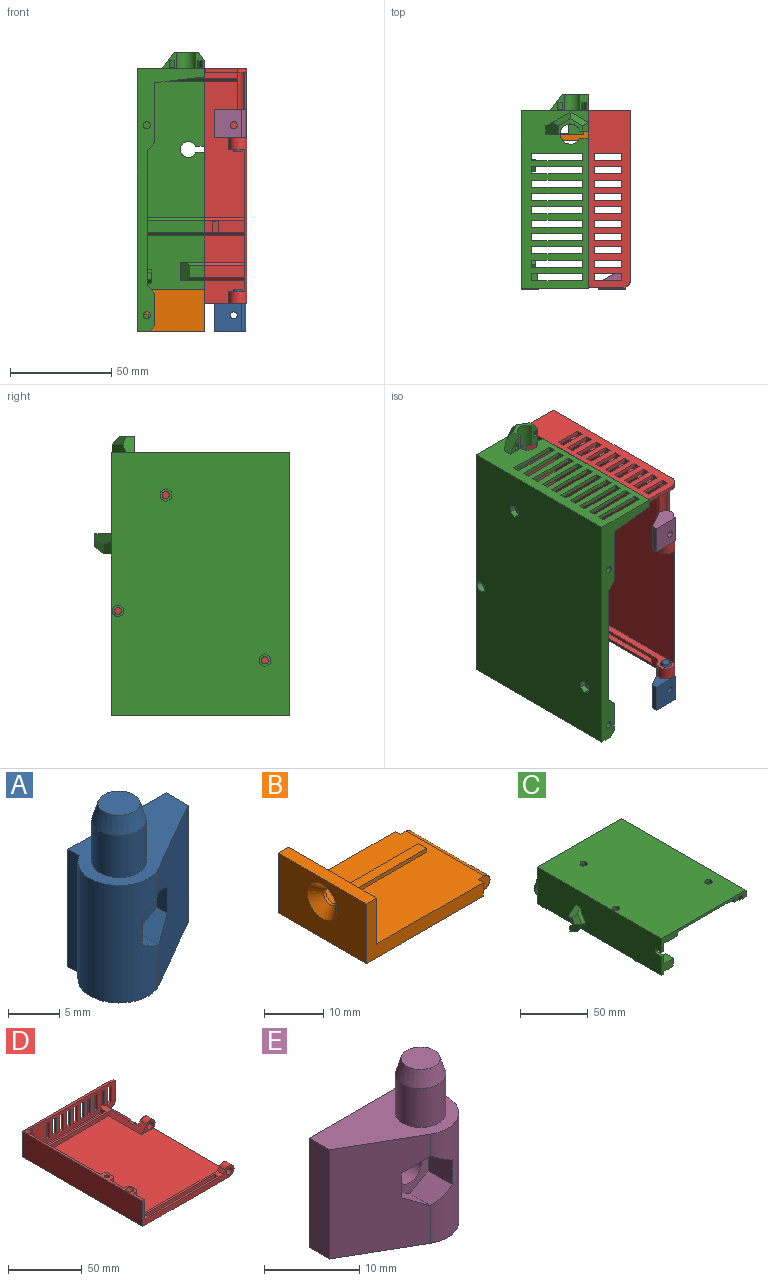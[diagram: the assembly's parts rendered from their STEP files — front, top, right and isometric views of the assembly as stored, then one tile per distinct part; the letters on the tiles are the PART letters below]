
ASSEMBLY  parts=5 mates=4
PART A: 18 faces, bbox 15.5x9x21 mm
  f0: cylinder r=4mm len=14mm, axis (0,0,1), area 161.7mm2, adj f1,f2,f5,f6,f11,f12,f15,f16
  f1: plane 14x9.51mm, normal (0.5,-0.87,0), area 138.4mm2, adj f0,f4,f5,f6,f12,f13,f14,f15
  f2: plane 14x1.55mm, normal (-1,0,0), area 21.7mm2, adj f0,f3,f5,f6
  f3: plane 14x13.53mm, normal (0,1,0), area 179.8mm2, adj f2,f4,f5,f6,f10
  f4: plane 14x3mm, normal (1,0,0), area 42mm2, adj f1,f3,f5,f6
  f5: plane 15.5x9mm, normal (0,0,-1), area 99.6mm2, adj f0,f1,f2,f3,f4
  f6: plane 15.5x9mm, normal (0,0,1), area 77.6mm2, adj f0,f1,f2,f3,f4,f7
  f7: cylinder r=2.65mm len=5.3mm, axis (0,0,-1), area 83.3mm2, adj f6,f9
  f8: plane 4.1x4.1mm, normal (0,0,1), area 13.2mm2, adj f9
  f9: cone r=2.05mm half-angle=16.7deg, axis (0,0,-1), area 30.8mm2, adj f7,f8
  f10: cylinder r=1.75mm len=5.41mm, axis (0,-1,0), area 59.5mm2, adj f3,f17
  f11: plane 3.52x3.18mm, normal (1,0,0.01), area 11.2mm2, adj f0,f12,f16,f17
  f12: plane 3.59x2.76mm, normal (0.5,0,0.87), area 11mm2, adj f0,f1,f11,f13,f17
  f13: plane 3.04x2.74mm, normal (-0.5,0,0.86), area 7.2mm2, adj f1,f12,f14,f17
  f14: plane 3.18x1.48mm, normal (-1,0,-0.01), area 4.7mm2, adj f1,f13,f15,f17
  f15: plane 3.06x2.76mm, normal (-0.5,0,-0.87), area 7.2mm2, adj f0,f1,f14,f16,f17
  f16: plane 3.59x2.74mm, normal (0.5,0,-0.86), area 11mm2, adj f0,f11,f15,f17
  f17: plane 6.35x5.52mm, normal (0,-1,0), area 16.6mm2, adj f10,f11,f12,f13,f14,f15,f16
PART B: 19 faces, bbox 30.7x21x12.3 mm
  f0: plane 26.8x21mm, normal (0,0,1), area 525mm2, adj f1,f2,f3,f5,f6,f7,f9,f10
  f1: plane 2.8x2.8mm, normal (0,1,0), area 7mm2, adj f0,f2,f8,f18
  f2: plane 2.8x1.2mm, normal (1,0,0), area 3.4mm2, adj f0,f1,f3,f8
  f3: plane 27.9x12.3mm, normal (0,1,0), area 101.9mm2, adj f0,f2,f4,f8,f14,f15
  f4: plane 21x12.3mm, normal (-1,0,0), area 219.8mm2, adj f3,f5,f8,f15,f17
  f5: plane 27.9x12.3mm, normal (0,-1,0), area 101.9mm2, adj f0,f4,f6,f8,f14,f15
  f6: plane 2.8x1.2mm, normal (1,0,0), area 3.4mm2, adj f0,f5,f7,f8
  f7: plane 2.8x2.8mm, normal (0,-1,0), area 7mm2, adj f0,f6,f8,f18
  f8: plane 29.3x21mm, normal (0,0,-1), area 611.9mm2, adj f1,f2,f3,f4,f5,f6,f7,f18
  f9: plane 17.2x0.8mm, normal (0,1,0), area 13.8mm2, adj f0,f10,f12,f13
  f10: plane 2x0.8mm, normal (-1,0,0), area 1.6mm2, adj f0,f9,f11,f13
  f11: plane 17.2x0.8mm, normal (0,-1,0), area 13.8mm2, adj f0,f10,f12,f13
  f12: plane 2x0.8mm, normal (1,0,0), area 1.6mm2, adj f0,f9,f11,f13
  f13: plane 17.2x2mm, normal (0,0,1), area 34.4mm2, adj f9,f10,f11,f12
  f14: plane 21x9.5mm, normal (1,0,0), area 191.5mm2, adj f0,f3,f5,f15,f16
  f15: plane 21x2.5mm, normal (0,0,1), area 52.5mm2, adj f3,f4,f5,f14
  f16: cylinder r=1.6mm len=3.2mm, axis (1,0,0), area 6mm2, adj f14,f17
  f17: cone r=1.6mm half-angle=45deg, axis (-1,0,0), area 43.1mm2, adj f4,f16
  f18: cylinder r=1.4mm len=18.6mm, axis (0,-1,0), area 81.8mm2, adj f0,f1,f7,f8
PART C: 219 faces, bbox 96x138x36.3 mm
  f0: plane 14.2x3.4mm, normal (0,-1,0), area 39.1mm2, adj f1,f3,f5,f205,f213,f214,f215
  f1: plane 14.2x5mm, normal (0,0,-1), area 55mm2, adj f0,f5,f205,f206,f214,f215,f216
  f2: plane 14.2x3.4mm, normal (0,1,0), area 39.1mm2, adj f3,f5,f207,f208,f209,f210,f211
  f3: plane 82x22.75mm, normal (0,0,-1), area 1628.8mm2, adj f0,f2,f4,f5,f11,f18,f154,f155
  f4: plane 88x12.75mm, normal (0,-1,0), area 261.8mm2, adj f3,f5,f11,f22,f30,f32,f140,f189
  f5: plane 47.25x31.3mm, normal (1,0,0), area 1103.9mm2, adj f0,f1,f2,f3,f4,f6,f14,f18
  f6: plane 83x70.25mm, normal (0,0,-1), area 5742.5mm2, adj f5,f7,f13,f14,f16,f142,f146,f149
  f7: plane 67.25x31.3mm, normal (1,0,0), area 2014.9mm2, adj f6,f12,f15,f16,f17,f19,f21,f26
  f8: plane 31.3x13mm, normal (0,-1,0), area 294.7mm2, adj f15,f33,f112,f113,f114,f170
  f9: cylinder r=1.75mm len=4mm, axis (-1,0,0), area 44mm2, adj f11,f32
  f10: cylinder r=1.75mm len=4mm, axis (-1,0,0), area 44mm2, adj f13,f32
  f11: plane 22.75x7.29mm, normal (-1,0,0), area 111.6mm2, adj f3,f4,f9,f18,f139,f140,f141,f154
  f12: plane 82x9mm, normal (0,0,-1), area 474.7mm2, adj f7,f13,f16,f17,f40,f41,f42,f43
  f13: plane 40.5x31.79mm, normal (-1,0,0), area 337.4mm2, adj f6,f10,f12,f15,f17,f25,f27,f33
  f14: plane 83x3mm, normal (0,1,0), area 249mm2, adj f5,f6,f38,f146
  f15: plane 82x14.5mm, normal (0,0,-1), area 1143.9mm2, adj f7,f8,f13,f17,f27,f114,f168,f169
  f16: plane 77x3mm, normal (0,-1,0), area 231mm2, adj f6,f7,f12,f150
  f17: plane 82x3mm, normal (0,1,0), area 246mm2, adj f7,f12,f13,f15
  f18: plane 82x3mm, normal (0,-1,0), area 246mm2, adj f3,f5,f11,f38
  f19: plane 10x4.25mm, normal (0,1,0), area 34.2mm2, adj f7,f21,f127,f131,f135,f136,f137,f138
  f20: plane 8x7mm, normal (0,1,0), area 23.9mm2, adj f22,f127,f131,f134,f135,f136,f137,f138
  f21: plane 88.62x14.5mm, normal (0,0,-1), area 250.1mm2, adj f5,f7,f19,f22,f31,f129,f131,f132
  f22: plane 130x33.3mm, normal (-1,0,0), area 4135.7mm2, adj f4,f20,f21,f25,f26,f30,f31,f127
  f23: plane 12x4.23mm, normal (1,0,0), area 36.5mm2, adj f26,f112,f115,f118,f119,f123,f124,f125
  f24: plane 8x7mm, normal (1,0,0), area 24mm2, adj f25,f112,f118,f122,f123,f124,f125,f126
  f25: plane 88x33.3mm, normal (0,1,0), area 1841.8mm2, adj f13,f22,f24,f26,f30,f32,f33,f73
  f26: plane 42.28x10mm, normal (0,0,-1), area 116.2mm2, adj f7,f22,f23,f25,f115,f116,f119,f128
  f27: plane 64.5x31.3mm, normal (0,-1,0), area 1143.9mm2, adj f13,f15,f33,f73,f74,f75,f76,f77
  f28: cylinder r=1.75mm len=4mm, axis (0,0,1), area 44mm2, adj f58,f65
  f29: cylinder r=1.75mm len=4mm, axis (0,0,1), area 44mm2, adj f51,f72
  f30: plane 130x88mm, normal (0,0,1), area 11361.1mm2, adj f4,f22,f25,f32,f59,f60,f61,f62
  f31: plane 17.05x11.7mm, normal (0,-1,0), area 103.7mm2, adj f5,f21,f22,f190,f200,f201,f204,f217
  f32: plane 130x33.3mm, normal (1,0,0), area 987.5mm2, adj f4,f9,f10,f25,f30,f33,f38,f139
  f33: plane 74.5x4mm, normal (0,0,-1), area 169mm2, adj f8,f13,f25,f27,f32,f113,f114,f145
  f34: plane 7.5x3mm, normal (1,0,0), area 22.5mm2, adj f35,f37,f38,f39
  f35: plane 59.7x3mm, normal (0,-1,0), area 179.1mm2, adj f34,f36,f38,f39
  f36: plane 7.5x3mm, normal (-1,0,0), area 22.5mm2, adj f35,f37,f38,f39
  f37: plane 59.7x3mm, normal (0,1,0), area 179.1mm2, adj f34,f36,f38,f39
  f38: plane 86x66.75mm, normal (0,0,-1), area 672.6mm2, adj f5,f14,f18,f32,f34,f35,f36,f37
  f39: plane 59.7x7.5mm, normal (0,0,-1), area 447.8mm2, adj f34,f35,f36,f37
  f40: plane 5x3mm, normal (1,0,0), area 15mm2, adj f12,f41,f43,f44
  f41: plane 43.77x3mm, normal (0,-1,0), area 131.3mm2, adj f12,f40,f42,f44
  f42: plane 5x3mm, normal (-1,0,0), area 15mm2, adj f12,f41,f43,f44
  f43: plane 43.77x3mm, normal (0,1,0), area 131.3mm2, adj f12,f40,f42,f44
  f44: plane 43.77x5mm, normal (0,0,-1), area 218.8mm2, adj f40,f41,f42,f43
  f45: plane 3.64x2mm, normal (0.98,0,-0.17), area 7mm2, adj f38,f46,f50,f51
  f46: plane 3.15x2.02mm, normal (0.49,0.85,-0.17), area 7mm2, adj f38,f45,f47,f51
  f47: plane 3.15x2.02mm, normal (-0.49,0.85,-0.17), area 7mm2, adj f38,f46,f48,f51
  f48: plane 3.64x2mm, normal (-0.98,0,-0.17), area 7mm2, adj f38,f47,f49,f51
  f49: plane 3.15x2.02mm, normal (-0.49,-0.85,-0.17), area 7mm2, adj f38,f48,f50,f51
  f50: plane 3.15x2.02mm, normal (0.49,-0.85,-0.17), area 7mm2, adj f38,f45,f49,f51
  f51: plane 6.47x5.6mm, normal (0,0,-1), area 17.5mm2, adj f29,f45,f46,f47,f48,f49,f50
  f52: plane 3.64x2mm, normal (-0.98,0,-0.17), area 7mm2, adj f12,f53,f57,f58
  f53: plane 3.15x2.02mm, normal (-0.49,-0.85,-0.17), area 7mm2, adj f12,f52,f54,f58
  f54: plane 3.15x2.02mm, normal (0.49,-0.85,-0.17), area 7mm2, adj f12,f53,f55,f58
  f55: plane 3.64x2mm, normal (0.98,0,-0.17), area 7mm2, adj f12,f54,f56,f58
  f56: plane 3.15x2.02mm, normal (0.49,0.85,-0.17), area 7mm2, adj f12,f55,f57,f58
  f57: plane 3.15x2.02mm, normal (-0.49,0.85,-0.17), area 7mm2, adj f12,f52,f56,f58
  f58: plane 6.47x5.6mm, normal (0,0,-1), area 17.5mm2, adj f28,f52,f53,f54,f55,f56,f57
  f59: plane 3.23x3mm, normal (1,0,0), area 9.7mm2, adj f30,f60,f64,f65
  f60: plane 3x2.8mm, normal (0.5,0.87,0), area 9.7mm2, adj f30,f59,f61,f65
  f61: plane 3x2.8mm, normal (-0.5,0.87,0), area 9.7mm2, adj f30,f60,f62,f65
  f62: plane 3.23x3mm, normal (-1,0,0), area 9.7mm2, adj f30,f61,f63,f65
  f63: plane 3x2.8mm, normal (-0.5,-0.87,0), area 9.7mm2, adj f30,f62,f64,f65
  f64: plane 3x2.8mm, normal (0.5,-0.87,0), area 9.7mm2, adj f30,f59,f63,f65
  f65: plane 6.47x5.6mm, normal (0,0,1), area 17.5mm2, adj f28,f59,f60,f61,f62,f63,f64
  f66: plane 3.23x3mm, normal (-1,0,0), area 9.7mm2, adj f30,f67,f71,f72
  f67: plane 3x2.8mm, normal (-0.5,-0.87,0), area 9.7mm2, adj f30,f66,f68,f72
  f68: plane 3x2.8mm, normal (0.5,-0.87,0), area 9.7mm2, adj f30,f67,f69,f72
  f69: plane 3.23x3mm, normal (1,0,0), area 9.7mm2, adj f30,f68,f70,f72
  f70: plane 3x2.8mm, normal (0.5,0.87,0), area 9.7mm2, adj f30,f69,f71,f72
  f71: plane 3x2.8mm, normal (-0.5,0.87,0), area 9.7mm2, adj f30,f66,f70,f72
  f72: plane 6.47x5.6mm, normal (0,0,1), area 17.5mm2, adj f29,f66,f67,f68,f69,f70,f71
  f73: plane 3.5x2mm, normal (0,0,1), area 7mm2, adj f25,f27,f74,f75
  f74: plane 25x2mm, normal (-1,0,0), area 50mm2, adj f25,f27,f73,f76
  f75: plane 25x2mm, normal (1,0,0), area 50mm2, adj f25,f27,f73,f76
  f76: plane 3.5x2mm, normal (0,0,-1), area 7mm2, adj f25,f27,f74,f75
  f77: plane 3.5x2mm, normal (0,0,1), area 7mm2, adj f25,f27,f78,f79
  f78: plane 25x2mm, normal (-1,0,0), area 50mm2, adj f25,f27,f77,f80
  f79: plane 25x2mm, normal (1,0,0), area 50mm2, adj f25,f27,f77,f80
  f80: plane 3.5x2mm, normal (0,0,-1), area 7mm2, adj f25,f27,f78,f79
  f81: plane 3.5x2mm, normal (0,0,1), area 7mm2, adj f25,f27,f82,f83
  f82: plane 25x2mm, normal (-1,0,0), area 50mm2, adj f25,f27,f81,f84
  f83: plane 25x2mm, normal (1,0,0), area 50mm2, adj f25,f27,f81,f84
  f84: plane 3.5x2mm, normal (0,0,-1), area 7mm2, adj f25,f27,f82,f83
  f85: plane 3.5x2mm, normal (0,0,1), area 7mm2, adj f25,f27,f86,f87
  f86: plane 25x2mm, normal (-1,0,0), area 50mm2, adj f25,f27,f85,f88
  f87: plane 25x2mm, normal (1,0,0), area 50mm2, adj f25,f27,f85,f88
  f88: plane 3.5x2mm, normal (0,0,-1), area 7mm2, adj f25,f27,f86,f87
  f89: plane 3.5x2mm, normal (0,0,1), area 7mm2, adj f25,f27,f90,f91
  f90: plane 25x2mm, normal (-1,0,0), area 50mm2, adj f25,f27,f89,f92
  f91: plane 25x2mm, normal (1,0,0), area 50mm2, adj f25,f27,f89,f92
  f92: plane 3.5x2mm, normal (0,0,-1), area 7mm2, adj f25,f27,f90,f91
  f93: plane 3.5x2mm, normal (0,0,1), area 7mm2, adj f25,f27,f94,f95
  f94: plane 25x2mm, normal (-1,0,0), area 50mm2, adj f25,f27,f93,f96
  f95: plane 25x2mm, normal (1,0,0), area 50mm2, adj f25,f27,f93,f96
  f96: plane 3.5x2mm, normal (0,0,-1), area 7mm2, adj f25,f27,f94,f95
  f97: plane 3.5x2mm, normal (0,0,1), area 7mm2, adj f25,f27,f98,f99
  f98: plane 25x2mm, normal (-1,0,0), area 50mm2, adj f25,f27,f97,f100
  f99: plane 25x2mm, normal (1,0,0), area 50mm2, adj f25,f27,f97,f100
  f100: plane 3.5x2mm, normal (0,0,-1), area 7mm2, adj f25,f27,f98,f99
  f101: plane 3.5x2mm, normal (0,0,1), area 7mm2, adj f25,f27,f102,f103
  f102: plane 25x2mm, normal (-1,0,0), area 50mm2, adj f25,f27,f101,f104
  f103: plane 25x2mm, normal (1,0,0), area 50mm2, adj f25,f27,f101,f104
  f104: plane 3.5x2mm, normal (0,0,-1), area 7mm2, adj f25,f27,f102,f103
  f105: plane 3.5x2mm, normal (0,0,1), area 7mm2, adj f25,f27,f106,f107
  f106: plane 25x2mm, normal (-1,0,0), area 50mm2, adj f25,f27,f105,f108
  f107: plane 25x2mm, normal (1,0,0), area 50mm2, adj f25,f27,f105,f108
  f108: plane 3.5x2mm, normal (0,0,-1), area 7mm2, adj f25,f27,f106,f107
  f109: plane 3.5x2mm, normal (0,0,1), area 7mm2, adj f13,f25,f27,f110
  f110: plane 25x2mm, normal (1,0,0), area 50mm2, adj f25,f27,f109,f111
  f111: plane 3.5x2mm, normal (0,0,-1), area 7mm2, adj f13,f25,f27,f110
  f112: cylinder r=5mm len=12mm, axis (0,1,0), area 224.8mm2, adj f8,f23,f24,f25,f113,f115,f118
  f113: plane 4.42x4mm, normal (-1,0,0), area 17.7mm2, adj f8,f25,f33,f112
  f114: plane 31.3x2mm, normal (1,0,0), area 62.6mm2, adj f8,f15,f27,f33
  f115: plane 9x3.5mm, normal (0,-1,0), area 19.2mm2, adj f23,f26,f112,f170
  f116: plane 9x5.2mm, normal (-0.87,0,-0.5), area 41.6mm2, adj f25,f26,f117,f120
  f117: plane 12x6.93mm, normal (-0.87,0,0.5), area 48.5mm2, adj f25,f116,f121,f122
  f118: plane 12x7.54mm, normal (0,1,0), area 28.8mm2, adj f23,f24,f112,f119,f120,f121,f122
  f119: plane 4.3x4mm, normal (0,0.6,-0.8), area 17.2mm2, adj f23,f26,f118,f120
  f120: plane 9x6.93mm, normal (-0.69,0.6,-0.4), area 43.3mm2, adj f116,f118,f119,f121
  f121: plane 9x6.93mm, normal (-0.69,0.6,0.4), area 43.3mm2, adj f117,f118,f120,f122
  f122: plane 8x6mm, normal (0,0.6,0.8), area 49.4mm2, adj f24,f25,f117,f118,f121
  f123: plane 16.26x8.2mm, normal (0,-1,0), area 47.5mm2, adj f23,f24,f124,f126
  f124: cylinder r=5.9mm len=11.61mm, axis (0,-1,0), area 59.6mm2, adj f23,f24,f123,f125
  f125: plane 16.26x8.2mm, normal (0,1,0), area 47.5mm2, adj f23,f24,f124,f126
  f126: cylinder r=8.2mm len=16.26mm, axis (0,-1,0), area 84.9mm2, adj f23,f24,f123,f125
  f127: cylinder r=4mm len=10mm, axis (-1,0,0), area 133.1mm2, adj f7,f19,f20,f22,f128,f131
  f128: plane 4.39x2mm, normal (0,-1,0), area 8.8mm2, adj f7,f22,f26,f127
  f129: plane 8x4.62mm, normal (0,-0.87,-0.5), area 37mm2, adj f21,f22,f130,f132
  f130: plane 11x6.35mm, normal (0,-0.87,0.5), area 43.9mm2, adj f22,f129,f133,f134
  f131: plane 13x6.54mm, normal (-1,0,0), area 28.5mm2, adj f19,f20,f21,f127,f132,f133,f134
  f132: plane 8.08x8mm, normal (-0.6,-0.69,-0.4), area 46.2mm2, adj f21,f129,f131,f133
  f133: plane 8x6.35mm, normal (-0.6,-0.69,0.4), area 37.5mm2, adj f130,f131,f132,f134
  f134: plane 8x6mm, normal (-0.6,0,0.8), area 45.2mm2, adj f20,f22,f130,f131,f133
  f135: plane 14.27x7.2mm, normal (1,0,0), area 40.5mm2, adj f19,f20,f136,f138
  f136: cylinder r=4.9mm len=9.6mm, axis (1,0,0), area 49mm2, adj f19,f20,f135,f137
  f137: plane 14.27x7.2mm, normal (-1,0,0), area 40.5mm2, adj f19,f20,f136,f138
  f138: cylinder r=7.2mm len=14.27mm, axis (1,0,0), area 74.3mm2, adj f19,f20,f135,f137
  f139: plane 4x3.8mm, normal (0,0.71,-0.71), area 21.5mm2, adj f11,f32,f38,f141
  f140: plane 4x2.8mm, normal (0,-0.71,-0.71), area 15.8mm2, adj f4,f11,f32,f141
  f141: plane 16.15x4mm, normal (0,0,-1), area 64.6mm2, adj f11,f32,f139,f140
  f142: plane 3x1mm, normal (0,-1,0), area 3mm2, adj f6,f13,f143,f146
  f143: plane 4x3.8mm, normal (0,-0.71,-0.71), area 21.5mm2, adj f13,f32,f38,f142,f144
  f144: plane 29.7x4mm, normal (0,0,-1), area 118.8mm2, adj f13,f32,f143,f145
  f145: plane 24.5x4mm, normal (0,-0.99,-0.12), area 98.7mm2, adj f13,f32,f33,f144
  f146: plane 55.25x3mm, normal (-1,0,0), area 165.7mm2, adj f6,f14,f38,f142
  f147: cylinder r=1.75mm len=3.5mm, axis (-1,0,0), area 16.5mm2, adj f156,f162
  f148: cylinder r=1.75mm len=3.5mm, axis (-1,0,0), area 16.5mm2, adj f150,f167
  f149: plane 6.19x5mm, normal (0,-1,0), area 31mm2, adj f6,f13,f150,f153
  f150: plane 9x6.19mm, normal (-1,0,0), area 40.1mm2, adj f6,f12,f16,f148,f149,f151,f152,f153
  f151: plane 5x3.19mm, normal (0,1,0), area 16mm2, adj f12,f13,f150,f152
  f152: plane 5x4.5mm, normal (0,0,-1), area 12.5mm2, adj f13,f150,f151,f153,f166,f167
  f153: plane 5x4.5mm, normal (0,0,-1), area 12.5mm2, adj f13,f149,f150,f152,f163,f167
  f154: plane 6.19x5mm, normal (0,-1,0), area 31mm2, adj f3,f11,f156,f157
  f155: plane 6.19x5mm, normal (0,1,0), area 31mm2, adj f3,f11,f156,f157
  f156: plane 9x6.19mm, normal (-1,0,0), area 46.1mm2, adj f3,f147,f154,f155,f157
  f157: plane 9x5mm, normal (0,0,-1), area 25mm2, adj f11,f154,f155,f156,f158,f159,f162
  f158: plane 5.04x3.5mm, normal (0,-1,0), area 17.6mm2, adj f11,f157,f161,f162
  f159: plane 5.04x3.5mm, normal (0,1,0), area 17.6mm2, adj f11,f157,f160,f162
  f160: plane 3.5x2.85mm, normal (0,0.5,-0.87), area 11.5mm2, adj f11,f159,f161,f162
  f161: plane 3.5x2.85mm, normal (0,-0.5,-0.87), area 11.5mm2, adj f11,f158,f160,f162
  f162: plane 6.68x5.7mm, normal (1,0,0), area 23.8mm2, adj f147,f157,f158,f159,f160,f161
  f163: plane 5.04x3.5mm, normal (0,1,0), area 17.6mm2, adj f13,f153,f164,f167
  f164: plane 3.5x2.85mm, normal (0,0.5,-0.87), area 11.5mm2, adj f13,f163,f165,f167
  f165: plane 3.5x2.85mm, normal (0,-0.5,-0.87), area 11.5mm2, adj f13,f164,f166,f167
  f166: plane 5.04x3.5mm, normal (0,-1,0), area 17.6mm2, adj f13,f152,f165,f167
  f167: plane 6.68x5.7mm, normal (1,0,0), area 23.8mm2, adj f148,f152,f153,f163,f164,f165,f166
  f168: plane 31.3x3mm, normal (0,-1,0), area 93.9mm2, adj f7,f15,f26,f169
  f169: plane 31.3x1.5mm, normal (0.71,-0.71,0), area 66.4mm2, adj f15,f26,f168,f170
  f170: plane 31.3x1mm, normal (1,0,0), area 31.3mm2, adj f8,f15,f26,f115,f169
  f171: plane 31.3x3mm, normal (0,-1,0), area 93.9mm2, adj f5,f6,f21,f172
  f172: plane 31.3x1.5mm, normal (0.71,-0.71,0), area 66.4mm2, adj f6,f21,f171,f173
  f173: plane 31.3x6mm, normal (1,0,0), area 187.8mm2, adj f6,f21,f172,f174
  f174: plane 31.3x1.5mm, normal (0.71,0.71,0), area 66.4mm2, adj f6,f21,f173,f175
  f175: plane 31.3x3mm, normal (0,1,0), area 93.9mm2, adj f6,f7,f21,f174
  f176: plane 12x3mm, normal (0,-1,0), area 31.5mm2, adj f5,f21,f180,f181
  f177: plane 12x3mm, normal (0,1,0), area 31.5mm2, adj f5,f21,f178,f181
  f178: plane 9x1.5mm, normal (0.71,0.71,0), area 17.5mm2, adj f21,f177,f179,f181
  f179: plane 7.5x6mm, normal (1,0,0), area 45mm2, adj f21,f178,f180,f181
  f180: plane 9x1.5mm, normal (0.71,-0.71,0), area 17.5mm2, adj f21,f176,f179,f181
  f181: plane 9x4.5mm, normal (0.71,0,0.71), area 54.1mm2, adj f5,f176,f177,f178,f179,f180
  f182: plane 2x2mm, normal (0,0,-1), area 3.1mm2, adj f185
  f183: plane 2x2mm, normal (0,0,-1), area 3.1mm2, adj f184
  f184: cone r=1mm half-angle=26.6deg, axis (0,0,1), area 36.9mm2, adj f21,f183
  f185: cone r=1mm half-angle=26.6deg, axis (0,0,1), area 36.9mm2, adj f26,f182
  f186: cylinder r=1.7mm len=30.1mm, axis (0,0,1), area 321.5mm2, adj f21,f187
  f187: plane 5.6x5.6mm, normal (0,0,1), area 15.6mm2, adj f186,f188
  f188: cylinder r=2.8mm len=5.6mm, axis (0,0,1), area 56.3mm2, adj f30,f187
  f189: plane 7x2mm, normal (0,0,-1), area 14mm2, adj f4,f5,f22,f191
  f190: plane 7x2mm, normal (0,0,1), area 14mm2, adj f5,f22,f31,f191
  f191: plane 3.5x2mm, normal (0,-1,0), area 7mm2, adj f5,f22,f189,f190
  f192: plane 18.2x0.8mm, normal (0,1,0), area 14.6mm2, adj f5,f193,f195,f196
  f193: plane 2x0.8mm, normal (0,0,1), area 1.6mm2, adj f5,f192,f194,f196
  f194: plane 18.2x0.8mm, normal (0,-1,0), area 14.6mm2, adj f5,f193,f195,f196
  f195: plane 2x0.8mm, normal (0,0,-1), area 1.6mm2, adj f5,f192,f194,f196
  f196: plane 18.2x2mm, normal (1,0,0), area 36.4mm2, adj f192,f193,f194,f195
  f197: plane 9.7x3.4mm, normal (0,-1,0), area 33mm2, adj f5,f198,f203,f204
  f198: plane 9.7x7.5mm, normal (0,0,1), area 66.6mm2, adj f5,f197,f199,f204,f218
  f199: plane 9.7x3.4mm, normal (0,1,0), area 33mm2, adj f5,f198,f200,f204
  f200: plane 9.7x8.5mm, normal (0,0,1), area 82.5mm2, adj f5,f31,f199,f204
  f201: plane 21x8.7mm, normal (0,0,-1), area 176.5mm2, adj f5,f31,f202,f217,f218
  f202: plane 9.7x7.2mm, normal (0,1,0), area 69.6mm2, adj f5,f201,f203,f204,f217
  f203: plane 9.7x5mm, normal (0,0,1), area 48.5mm2, adj f5,f197,f202,f204
  f204: plane 21x6.2mm, normal (1,0,0), area 104.7mm2, adj f31,f197,f198,f199,f200,f202,f203,f217
  f205: plane 5x3.4mm, normal (1,0,0), area 17mm2, adj f0,f1,f3,f206
  f206: plane 14.2x3.4mm, normal (0,1,0), area 48.3mm2, adj f1,f3,f5,f205
  f207: plane 8.5x3.4mm, normal (1,0,0), area 28.9mm2, adj f2,f3,f4,f208
  f208: plane 14.2x8.5mm, normal (0,0,-1), area 90.7mm2, adj f2,f4,f5,f207,f209,f210,f212
  f209: plane 7.5x1.79mm, normal (-0.97,0,-0.24), area 13.8mm2, adj f2,f208,f211,f212
  f210: plane 7.5x1.79mm, normal (0.97,0,-0.24), area 13.8mm2, adj f2,f208,f211,f212
  f211: cylinder r=1.6mm len=7.5mm, axis (0,-1,0), area 31.8mm2, adj f2,f209,f210,f212
  f212: plane 4x3mm, normal (0,1,0), area 9.1mm2, adj f208,f209,f210,f211
  f213: cylinder r=1.6mm len=4mm, axis (0,-1,0), area 17mm2, adj f0,f214,f215,f216
  f214: plane 4x1.79mm, normal (-0.97,0,-0.24), area 7.4mm2, adj f0,f1,f213,f216
  f215: plane 4x1.79mm, normal (0.97,0,-0.24), area 7.4mm2, adj f0,f1,f213,f216
  f216: plane 4x3mm, normal (0,-1,0), area 9.1mm2, adj f1,f213,f214,f215
  f217: cylinder r=1mm len=21mm, axis (0,-1,0), area 33mm2, adj f31,f201,f202,f204
  f218: cylinder r=1.4mm len=3.8mm, axis (0,0,-1), area 33.4mm2, adj f198,f201
PART D: 106 faces, bbox 87.5x116x21 mm
  f0: plane 87.5x21mm, normal (0,1,0), area 1359.7mm2, adj f1,f6,f10,f18,f19,f45,f46,f47
  f1: plane 116x83mm, normal (0,0,1), area 432.7mm2, adj f0,f4,f12,f13,f14,f15,f16,f17
  f2: plane 101.5x83.83mm, normal (0,0,1), area 8073mm2, adj f3,f8,f12,f14,f15,f16,f23,f24
  f3: plane 31.7x6.29mm, normal (-0.78,0,0.62), area 156.1mm2, adj f2,f6,f11,f78,f86,f89,f92,f93
  f4: plane 81x21mm, normal (0,-1,0), area 1128.9mm2, adj f1,f5,f6,f7,f9,f10,f18,f21
  f5: plane 67.27x5mm, normal (0,0,1), area 334.7mm2, adj f4,f21,f22,f101,f102,f103
  f6: plane 76.5x25.4mm, normal (0,0,1), area 171.3mm2, adj f0,f3,f4,f7,f16,f20,f22,f77
  f7: cylinder r=4.5mm len=32.2mm, axis (0,-1,0), area 123.9mm2, adj f4,f6,f9,f11,f78,f92,f93,f94
  f8: plane 85.5x8mm, normal (0,1,0), area 305mm2, adj f2,f15,f85,f86,f87,f95
  f9: plane 32.2x0.53mm, normal (0,0,1), area 17mm2, adj f4,f7,f11,f90
  f10: plane 116x83mm, normal (0,0,-1), area 9553.9mm2, adj f0,f4,f11,f17,f19,f86,f90,f91
  f11: plane 10.24x9mm, normal (0,1,0), area 39.7mm2, adj f3,f7,f9,f10,f78,f86,f88,f90
  f12: plane 20x6mm, normal (1,0,0), area 104.3mm2, adj f1,f2,f28,f29,f38,f39,f41,f42
  f13: cylinder r=1.73mm len=4mm, axis (0,0,1), area 43.4mm2, adj f1,f38
  f14: plane 20x13mm, normal (1,0,0), area 260mm2, adj f1,f2,f23,f30
  f15: plane 20x11.25mm, normal (1,0,0), area 204mm2, adj f1,f2,f8,f17,f27,f95
  f16: plane 67.25x20mm, normal (1,0,0), area 1338mm2, adj f1,f2,f6,f20,f31,f104
  f17: plane 87.5x21mm, normal (0,-1,0), area 429.9mm2, adj f1,f10,f15,f19,f85,f86,f87,f95
  f18: plane 15.87x2mm, normal (1,0,0), area 31.7mm2, adj f0,f4,f91,f105
  f19: plane 116x21mm, normal (-1,0,0), area 2436mm2, adj f0,f1,f10,f17
  f20: plane 16.5x3mm, normal (0,-1,0), area 49.5mm2, adj f1,f6,f16,f22
  f21: plane 20x3mm, normal (1,0,0), area 60mm2, adj f1,f4,f5,f22
  f22: plane 20x1.5mm, normal (0.71,-0.71,0), area 37.5mm2, adj f1,f5,f6,f20,f21,f103
  f23: plane 20x3mm, normal (0,1,0), area 60mm2, adj f1,f2,f14,f24
  f24: plane 20x1.5mm, normal (0.71,0.71,0), area 42.4mm2, adj f1,f2,f23,f25
  f25: plane 20x6mm, normal (1,0,0), area 120mm2, adj f1,f2,f24,f26
  f26: plane 20x1.5mm, normal (0.71,-0.71,0), area 42.4mm2, adj f1,f2,f25,f27
  f27: plane 20x3mm, normal (0,-1,0), area 60mm2, adj f1,f2,f15,f26
  f28: plane 20x1.5mm, normal (0.71,0.71,0), area 42.4mm2, adj f1,f2,f12,f31
  f29: plane 20x1.5mm, normal (0.71,-0.71,0), area 42.4mm2, adj f1,f2,f12,f30
  f30: plane 20x3mm, normal (0,-1,0), area 60mm2, adj f1,f2,f14,f29
  f31: plane 20x3mm, normal (0,1,0), area 60mm2, adj f1,f2,f16,f28
  f32: cylinder r=2.75mm len=5.5mm, axis (0,0,1), area 1.7mm2, adj f1,f37
  f33: plane 2.4x2.4mm, normal (0,0,1), area 4.5mm2, adj f37
  f34: cylinder r=2.75mm len=5.5mm, axis (0,0,1), area 1.7mm2, adj f1,f36
  f35: plane 2.4x2.4mm, normal (0,0,1), area 4.5mm2, adj f36
  f36: cone r=1.2mm half-angle=27.3deg, axis (0,0,1), area 41.9mm2, adj f34,f35
  f37: cone r=1.2mm half-angle=27.3deg, axis (0,0,1), area 41.9mm2, adj f32,f33
  f38: plane 5.9x5.6mm, normal (0,0,-1), area 23.7mm2, adj f12,f13,f40,f41,f42
  f39: plane 5.9x5.6mm, normal (0,0,1), area 23.7mm2, adj f12,f40,f41,f42,f44
  f40: plane 5.6x2.8mm, normal (1,0,0), area 15.7mm2, adj f38,f39,f41,f42
  f41: plane 5.9x2.8mm, normal (0,1,0), area 16.5mm2, adj f12,f38,f39,f40
  f42: plane 5.9x2.8mm, normal (0,-1,0), area 16.5mm2, adj f12,f38,f39,f40
  f43: plane 3.46x3.46mm, normal (0,0,1), area 9.4mm2, adj f44
  f44: cylinder r=1.73mm len=13.2mm, axis (0,0,1), area 143.3mm2, adj f39,f43
  f45: plane 13.5x2mm, normal (1,0,0), area 27mm2, adj f0,f4,f46,f47
  f46: plane 3.5x2mm, normal (0,0,1), area 7mm2, adj f0,f4,f45,f48
  f47: plane 3.5x2mm, normal (0,0,-1), area 7mm2, adj f0,f4,f45,f48
  f48: plane 13.5x2mm, normal (-1,0,0), area 27mm2, adj f0,f4,f46,f47
  f49: plane 13.5x2mm, normal (1,0,0), area 27mm2, adj f0,f4,f50,f51
  f50: plane 3.5x2mm, normal (0,0,1), area 7mm2, adj f0,f4,f49,f52
  f51: plane 3.5x2mm, normal (0,0,-1), area 7mm2, adj f0,f4,f49,f52
  f52: plane 13.5x2mm, normal (-1,0,0), area 27mm2, adj f0,f4,f50,f51
  f53: plane 13.5x2mm, normal (1,0,0), area 27mm2, adj f0,f4,f54,f55
  f54: plane 3.5x2mm, normal (0,0,1), area 7mm2, adj f0,f4,f53,f56
  f55: plane 3.5x2mm, normal (0,0,-1), area 7mm2, adj f0,f4,f53,f56
  f56: plane 13.5x2mm, normal (-1,0,0), area 27mm2, adj f0,f4,f54,f55
  f57: plane 13.5x2mm, normal (1,0,0), area 27mm2, adj f0,f4,f58,f59
  f58: plane 3.5x2mm, normal (0,0,1), area 7mm2, adj f0,f4,f57,f60
  f59: plane 3.5x2mm, normal (0,0,-1), area 7mm2, adj f0,f4,f57,f60
  f60: plane 13.5x2mm, normal (-1,0,0), area 27mm2, adj f0,f4,f58,f59
  f61: plane 13.5x2mm, normal (1,0,0), area 27mm2, adj f0,f4,f62,f63
  f62: plane 3.5x2mm, normal (0,0,1), area 7mm2, adj f0,f4,f61,f64
  f63: plane 3.5x2mm, normal (0,0,-1), area 7mm2, adj f0,f4,f61,f64
  f64: plane 13.5x2mm, normal (-1,0,0), area 27mm2, adj f0,f4,f62,f63
  f65: plane 13.5x2mm, normal (1,0,0), area 27mm2, adj f0,f4,f66,f67
  f66: plane 3.5x2mm, normal (0,0,1), area 7mm2, adj f0,f4,f65,f68
  f67: plane 3.5x2mm, normal (0,0,-1), area 7mm2, adj f0,f4,f65,f68
  f68: plane 13.5x2mm, normal (-1,0,0), area 27mm2, adj f0,f4,f66,f67
  f69: plane 13.5x2mm, normal (1,0,0), area 27mm2, adj f0,f4,f70,f71
  f70: plane 3.5x2mm, normal (0,0,1), area 7mm2, adj f0,f4,f69,f72
  f71: plane 3.5x2mm, normal (0,0,-1), area 7mm2, adj f0,f4,f69,f72
  f72: plane 13.5x2mm, normal (-1,0,0), area 27mm2, adj f0,f4,f70,f71
  f73: plane 13.5x2mm, normal (1,0,0), area 27mm2, adj f0,f4,f74,f75
  f74: plane 3.5x2mm, normal (0,0,1), area 7mm2, adj f0,f4,f73,f76
  f75: plane 3.5x2mm, normal (0,0,-1), area 7mm2, adj f0,f4,f73,f76
  f76: plane 13.5x2mm, normal (-1,0,0), area 27mm2, adj f0,f4,f74,f75
  f77: plane 13.5x2mm, normal (1,0,0), area 27mm2, adj f0,f4,f6,f79
  f78: plane 3.6x1.24mm, normal (0,0,1), area 4.4mm2, adj f3,f7,f11,f93
  f79: plane 3.5x2mm, normal (0,0,-1), area 7mm2, adj f0,f4,f77,f80
  f80: plane 13.5x2mm, normal (-1,0,0), area 27mm2, adj f0,f4,f6,f79
  f81: plane 13.5x2mm, normal (1,0,0), area 27mm2, adj f0,f4,f82,f83
  f82: plane 3.5x2mm, normal (0,0,1), area 7mm2, adj f0,f4,f81,f84
  f83: plane 3.5x2mm, normal (0,0,-1), area 7mm2, adj f0,f4,f81,f84
  f84: plane 13.5x2mm, normal (-1,0,0), area 27mm2, adj f0,f4,f82,f83
  f85: plane 6x2.79mm, normal (-0.78,0,0.62), area 21.3mm2, adj f8,f17,f86,f95
  f86: cylinder r=4.5mm len=81.8mm, axis (0,-1,0), area 431.8mm2, adj f2,f3,f8,f10,f11,f17,f85,f89
  f87: cylinder r=2.85mm len=6mm, axis (0,-1,0), area 107.4mm2, adj f8,f17
  f88: cylinder r=2.85mm len=6mm, axis (0,1,0), area 107.4mm2, adj f11,f89
  f89: plane 13x8mm, normal (0,-1,0), area 46.4mm2, adj f2,f3,f86,f88
  f90: plane 32.2x1mm, normal (1,0,0), area 32.2mm2, adj f4,f9,f10,f11
  f91: cylinder r=4.5mm len=4.5mm, axis (0,-1,0), area 14.1mm2, adj f0,f4,f10,f18
  f92: plane 2.14x1mm, normal (0,-1,0), area 1.7mm2, adj f3,f6,f7,f94
  f93: plane 2.14x1mm, normal (0,1,0), area 1.7mm2, adj f3,f7,f78,f94
  f94: plane 5.2x2.14mm, normal (0,0,1), area 11.1mm2, adj f3,f7,f92,f93
  f95: plane 75.27x6mm, normal (0,0,1), area 249.8mm2, adj f8,f15,f17,f85,f96,f97,f98,f99
  f96: plane 67.27x3.5mm, normal (0,-1,0), area 235.4mm2, adj f95,f97,f98,f100
  f97: plane 3.5x3mm, normal (-1,0,0), area 10.5mm2, adj f95,f96,f99,f100
  f98: plane 3.5x3mm, normal (1,0,0), area 10.5mm2, adj f95,f96,f99,f100
  f99: plane 67.27x3.5mm, normal (0,1,0), area 235.4mm2, adj f95,f97,f98,f100
  f100: plane 67.27x3mm, normal (0,0,1), area 201.8mm2, adj f96,f97,f98,f99
  f101: plane 5x3.5mm, normal (-1,0,0), area 17.5mm2, adj f4,f5,f6,f102
  f102: plane 67.27x3.5mm, normal (0,1,0), area 235.4mm2, adj f5,f6,f101,f103
  f103: plane 3.5x1.5mm, normal (1,0,0), area 5.3mm2, adj f5,f6,f22,f102
  f104: plane 75.27x3.5mm, normal (0,-1,0), area 258.6mm2, adj f2,f3,f6,f16
  f105: cylinder r=16.5mm len=4.5mm, axis (0,1,0), area 9.1mm2, adj f0,f1,f4,f18
PART E: 18 faces, bbox 15.5x9x21 mm
  f0: cylinder r=4mm len=14mm, axis (0,0,1), area 161.7mm2, adj f1,f2,f5,f6,f11,f12,f15,f16
  f1: plane 14x9.51mm, normal (-0.5,-0.87,0), area 138.4mm2, adj f0,f4,f5,f6,f12,f13,f14,f15
  f2: plane 14x1.55mm, normal (1,0,0), area 21.7mm2, adj f0,f3,f5,f6
  f3: plane 14x13.53mm, normal (0,1,0), area 179.8mm2, adj f2,f4,f5,f6,f10
  f4: plane 14x3mm, normal (-1,0,0), area 42mm2, adj f1,f3,f5,f6
  f5: plane 15.5x9mm, normal (0,0,-1), area 99.6mm2, adj f0,f1,f2,f3,f4
  f6: plane 15.5x9mm, normal (0,0,1), area 77.6mm2, adj f0,f1,f2,f3,f4,f7
  f7: cylinder r=2.65mm len=5.3mm, axis (0,0,-1), area 83.3mm2, adj f6,f9
  f8: plane 4.1x4.1mm, normal (0,0,1), area 13.2mm2, adj f9
  f9: cone r=2.05mm half-angle=16.7deg, axis (0,0,-1), area 30.8mm2, adj f7,f8
  f10: cylinder r=1.75mm len=5.41mm, axis (0,-1,0), area 59.5mm2, adj f3,f17
  f11: plane 3.52x3.18mm, normal (-1,0,0.01), area 11.2mm2, adj f0,f12,f16,f17
  f12: plane 3.59x2.76mm, normal (-0.5,0,0.87), area 11mm2, adj f0,f1,f11,f13,f17
  f13: plane 3.04x2.74mm, normal (0.5,0,0.86), area 7.2mm2, adj f1,f12,f14,f17
  f14: plane 3.18x1.48mm, normal (1,0,-0.01), area 4.7mm2, adj f1,f13,f15,f17
  f15: plane 3.06x2.76mm, normal (0.5,0,-0.87), area 7.2mm2, adj f0,f1,f14,f16,f17
  f16: plane 3.59x2.74mm, normal (-0.5,0,-0.86), area 11mm2, adj f0,f11,f15,f17
  f17: plane 6.35x5.52mm, normal (0,-1,0), area 16.6mm2, adj f10,f11,f12,f13,f14,f15,f16
PLACE A rot(axis=(0,0,-1),180deg) t=(75.95,-103.85,-26.64)mm fixed
PLACE B rot(axis=(0,-0.71,-0.71),180deg) t=(-43.93,-40.2,24.72)mm
PLACE C rot(axis=(0.58,-0.58,-0.58),120deg) t=(11.65,-79.95,24.72)mm
PLACE D rot(axis=(0.58,-0.58,-0.58),120deg) t=(65.95,70.87,24.72)mm
PLACE E rot(axis=(1,0,0),180deg) t=(75.95,-103.85,55.36)mm
MATE fastened E.f10 <-> A.f3  axis (0,-1,0) through (59.45,-116.5,61.36)mm
MATE fastened A.f10 <-> C.f32  axis (0,-1,0) through (59.45,-116.5,-32.64)mm
MATE revolute A.f0 <-> D.f7  axis (0,0,1) through (61.45,-111.5,-26.64)mm
MATE fastened C.f218 <-> B.f16  axis (1,0,0) through (42.45,-35.4,-30.14)mm
